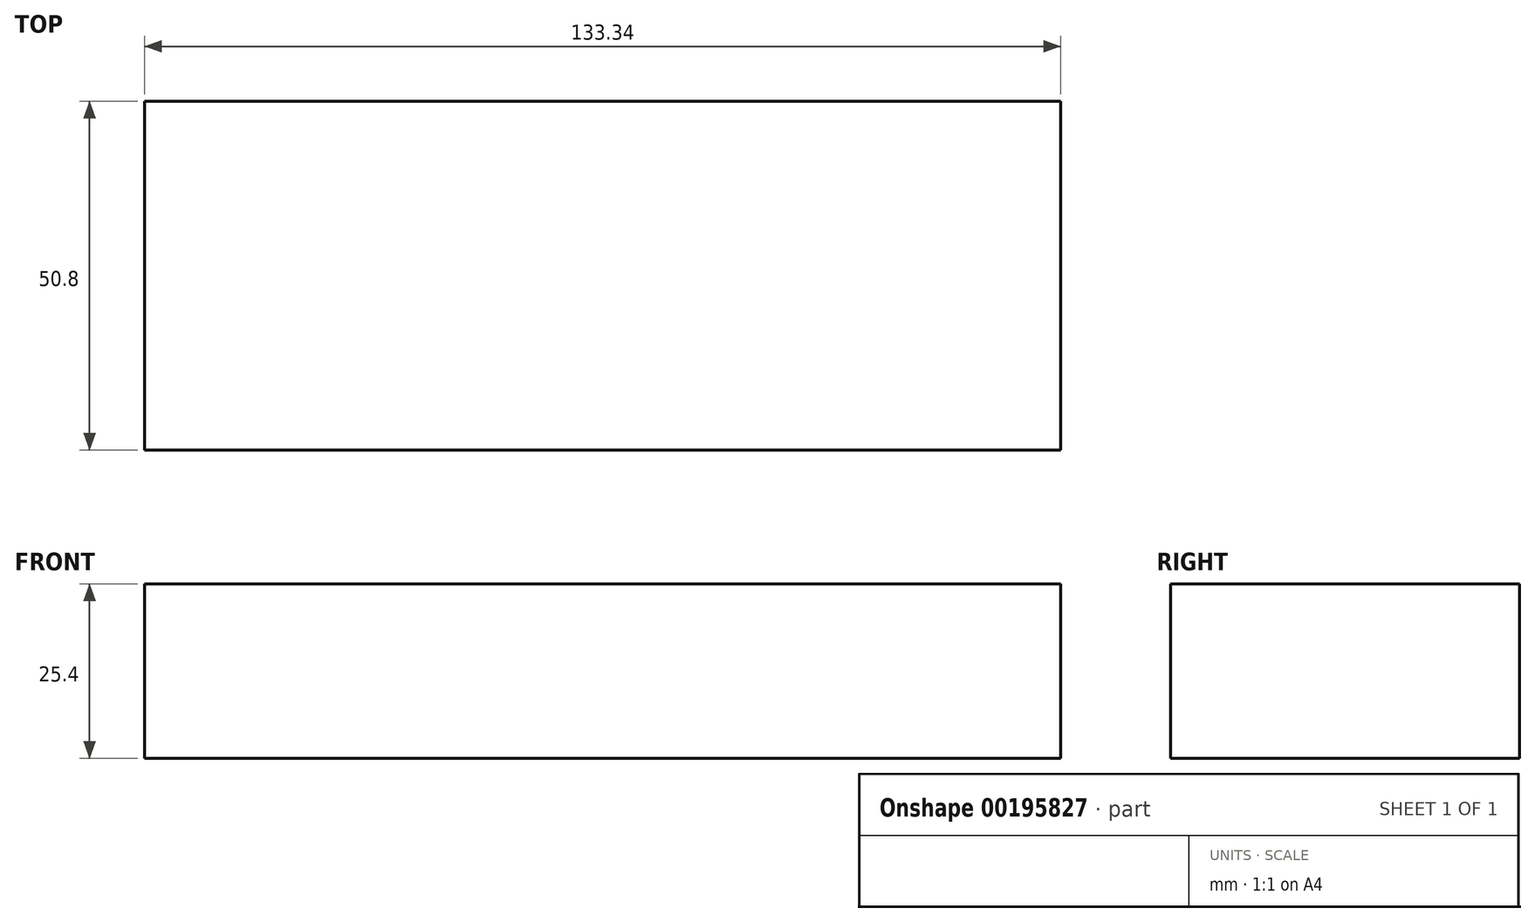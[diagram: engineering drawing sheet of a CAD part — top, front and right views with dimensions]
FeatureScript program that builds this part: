
annotation { "Feature Type Name" : "Feature", "Feature Type Description" : "" }
export const myFeature = defineFeature(function(context is Context, id is Id, definition is map)
    precondition{}
    {
        {
            var Q0;
            Q0=qCreatedBy(makeId("Top.planeOp"),FACE);
            var sketch = newSketch(context, id + "F0", { "sketchPlane" : qUnion([Q0])});
            skLineSegment(sketch, "E0.bottom", {"start": v(-66.67, 25.4) * mm, "end": v(66.68, 25.4) * mm});
            skLineSegment(sketch, "E0.top", {"start": v(-66.68, -25.4) * mm, "end": v(66.67, -25.4) * mm});
            skLineSegment(sketch, "E0.left", {"start": v(-66.67, 25.4) * mm, "end": v(-66.68, -25.4) * mm});
            skLineSegment(sketch, "E0.right", {"start": v(66.68, 25.4) * mm, "end": v(66.67, -25.4) * mm});
            skPoint(sketch, "E0.middle", {"position": v(0, 0) * mm});
            skSolve(sketch);
        }
        {
            var Q0;
            Q0=makeQuery(id+"F0.imprint","IMPRINT",FACE,{"disambiguationData":[TD([[makeQuery(id+"F0.imprint","IMPRINT",EDGE,{"derivedFrom":sQuery(id+"F0.wireOp",EDGE,"E0.bottom")}),-1.0]])]});
            extrude(context, id + "F1", {"entities" : qUnion([Q0]), "depth" : 25.4 * mm});
        }
    });
